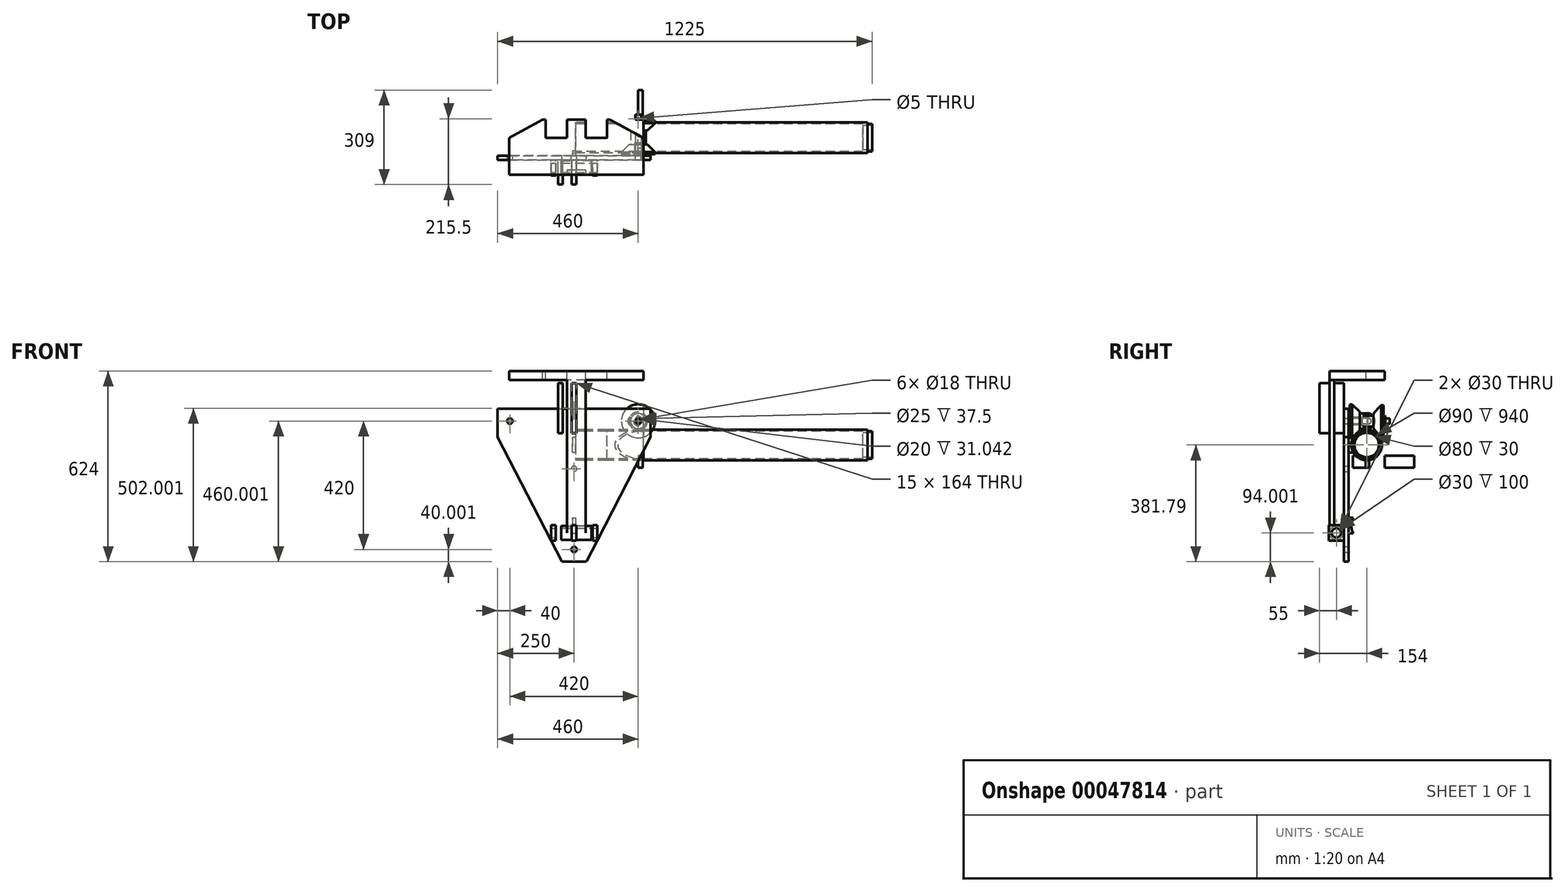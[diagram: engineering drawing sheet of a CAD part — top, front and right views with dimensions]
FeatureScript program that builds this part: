
annotation { "Feature Type Name" : "Feature", "Feature Type Description" : "" }
export const myFeature = defineFeature(function(context is Context, id is Id, definition is map)
    precondition{}
    {
        {
            var Q0;
            Q0=qCreatedBy(makeId("Right.planeOp"),FACE);
            var sketch = newSketch(context, id + "F0", { "sketchPlane" : qUnion([Q0])});
            skCircle(sketch, "E0", {"center": v(0, 0) * mm, "radius": 50 * mm});
            skCircle(sketch, "E1", {"center": v(0, 0) * mm, "radius": 45 * mm});
            skSolve(sketch);
        }
        {
            var Q0;
            Q0 = qSketchRegion(id + "F0", true);
            var Q1;
            Q1=sQuery(id+"F0.wireOp",EDGE,"E0");
            extrude(context, id + "F1", {"entities" : qUnion([Q0]), "surfaceEntities" : qUnion([Q1]), "endBound" : BoundingType.SYMMETRIC, "depth" : 1500 * mm});
        }
        {
            var Q0;
            Q0=qCreatedBy(makeId("Right.planeOp"),FACE);
            var sketch = newSketch(context, id + "F2", { "sketchPlane" : qUnion([Q0])});
            skLineSegment(sketch, "E2", {"start": v(0, 78.21) * mm, "end": v(121.58, 78.21) * mm, "construction": true});
            skLineSegment(sketch, "E3", {"start": v(0, 78.21) * mm, "end": v(0, 0) * mm, "construction": true});
            skLineSegment(sketch, "E4", {"start": v(-55, 65.71) * mm, "end": v(55, 65.71) * mm});
            skLineSegment(sketch, "E5", {"start": v(55, 65.71) * mm, "end": v(55, 23.21) * mm});
            skLineSegment(sketch, "E6", {"start": v(55, 23.21) * mm, "end": v(47.5, 23.21) * mm});
            skLineSegment(sketch, "E7", {"start": v(47.5, 23.21) * mm, "end": v(22.5, 48.21) * mm});
            skLineSegment(sketch, "E8", {"start": v(22.5, 48.21) * mm, "end": v(22.5, 53.21) * mm});
            skLineSegment(sketch, "E9", {"start": v(22.5, 53.21) * mm, "end": v(-22.5, 53.21) * mm});
            skLineSegment(sketch, "E10", {"start": v(-22.5, 53.21) * mm, "end": v(-22.5, 48.21) * mm});
            skLineSegment(sketch, "E11", {"start": v(-22.5, 48.21) * mm, "end": v(-47.5, 23.21) * mm});
            skLineSegment(sketch, "E12", {"start": v(-47.5, 23.21) * mm, "end": v(-55, 23.21) * mm});
            skLineSegment(sketch, "E13", {"start": v(-55, 23.21) * mm, "end": v(-55, 65.71) * mm});
            skPoint(sketch, "E14", {"position": v(0, 65.71) * mm});
            skLineSegment(sketch, "E15", {"start": v(-17.5, 65.71) * mm, "end": v(-17.5, 68.21) * mm});
            skLineSegment(sketch, "E16", {"start": v(-17.5, 68.21) * mm, "end": v(17.5, 68.21) * mm});
            skLineSegment(sketch, "E17", {"start": v(17.5, 68.21) * mm, "end": v(17.5, 65.71) * mm});
            skSolve(sketch);
        }
        {
            var Q0;
            {var subQ1=sQuery(id+"F2.wireOp",EDGE,"E15");Q0=makeQuery(id+"F2.imprint","IMPRINT",FACE,{"disambiguationData":[TD([[makeQuery(id+"F2.imprint","IMPRINT",EDGE,{"derivedFrom":subQ1}),-1.0]])]});}
            var Q1;
            {var subQ1=sQuery(id+"F2.wireOp",EDGE,"E5");Q1=makeQuery(id+"F2.imprint","IMPRINT",FACE,{"disambiguationData":[TD([[makeQuery(id+"F2.imprint","IMPRINT",EDGE,{"derivedFrom":subQ1}),-1.0]])]});}
            var Q2;
            Q2=sQuery(id+"F2.wireOp",EDGE,"E2");
            revolve(context, id + "F3", {"entities" : qUnion([Q0, Q1]), "axis" : qUnion([Q2]), "revolveType" : RevolveType.FULL});
        }
        {
            var Q0;
            {var subQ1=sQuery(id+"F2.wireOp",EDGE,"E5");Q0=makeQuery(id+"F2.imprint","IMPRINT",FACE,{"disambiguationData":[TD([[makeQuery(id+"F2.imprint","IMPRINT",EDGE,{"derivedFrom":subQ1}),-1.0]])]});}
            var sketch = newSketch(context, id + "F4", { "sketchPlane" : qUnion([Q0])});
            skLineSegment(sketch, "E18.0", {"start": v(0, 78.21) * mm, "end": v(121.58, 78.21) * mm});
            skLineSegment(sketch, "E19.1", {"start": v(-55, 65.71) * mm, "end": v(55, 65.71) * mm});
            skLineSegment(sketch, "E20.2", {"start": v(-17.5, 65.71) * mm, "end": v(-17.5, 68.21) * mm});
            skLineSegment(sketch, "E21", {"start": v(-55, 65.71) * mm, "end": v(-56, 65.71) * mm});
            skLineSegment(sketch, "E22", {"start": v(-56, 65.71) * mm, "end": v(-56, 69.21) * mm});
            skLineSegment(sketch, "E23", {"start": v(-56, 69.21) * mm, "end": v(-17.5, 69.21) * mm});
            skLineSegment(sketch, "E24", {"start": v(-17.5, 69.21) * mm, "end": v(-17.5, 68.21) * mm});
            skSolve(sketch);
        }
        {
            var Q0;
            {var subQ1=sQuery(id+"F4.wireOp",EDGE,"E20.2");Q0=makeQuery(id+"F4.imprint","IMPRINT",FACE,{"disambiguationData":[TD([[makeQuery(id+"F4.imprint","IMPRINT",EDGE,{"derivedFrom":subQ1}),1.0]])]});}
            var Q1;
            Q1=sQuery(id+"F4.wireOp",EDGE,"E18.0");
            revolve(context, id + "F5", {"entities" : qUnion([Q0]), "axis" : qUnion([Q1]), "revolveType" : RevolveType.FULL});
        }
        {
            var Q0;
            Q0=makeQuery(id+"F5.opRevolve","SWEPT_EDGE",EDGE,{"disambiguationData":[OSD([sQuery(id+"F4.wireOp",EDGE,"E22"),sQuery(id+"F4.wireOp",EDGE,"E23")])]});
            var Q1;
            Q1=makeQuery(id+"F5.opRevolve","SWEPT_EDGE",EDGE,{"disambiguationData":[OSD([sQuery(id+"F4.wireOp",EDGE,"E23"),sQuery(id+"F4.wireOp",EDGE,"E24")])]});
            var Q2;
            Q2=makeQuery(id+"F5.opRevolve","SWEPT_EDGE",EDGE,{"disambiguationData":[OSD([sQuery(id+"F4.wireOp",EDGE,"E19.1"),sQuery(id+"F4.wireOp",EDGE,"E20.2")])]});
            var Q3;
            Q3=makeQuery(id+"F5.opRevolve","SWEPT_EDGE",EDGE,{"disambiguationData":[OSD([sQuery(id+"F4.wireOp",EDGE,"E21"),sQuery(id+"F4.wireOp",EDGE,"E22")])]});
            chamfer(context, id + "F6", {"entities" : qUnion([Q0, Q1, Q2, Q3]), "width" : .5 * mm, "tangentPropagation" : true});
        }
        {
            var Q0;
            Q0=qCreatedBy(makeId("Right.planeOp"),FACE);
            var sketch = newSketch(context, id + "F7", { "sketchPlane" : qUnion([Q0])});
            skCircle(sketch, "E25.0", {"center": v(0, 0) * mm, "radius": 50 * mm});
            skLineSegment(sketch, "E26", {"start": v(35.7, -35) * mm, "end": v(155, -35) * mm});
            skLineSegment(sketch, "E27", {"start": v(-35.7, -35) * mm, "end": v(-45, -35) * mm});
            skLineSegment(sketch, "E28", {"start": v(-45, -35) * mm, "end": v(-45, -75) * mm});
            skLineSegment(sketch, "E29", {"start": v(-45, -75) * mm, "end": v(155, -75) * mm});
            skLineSegment(sketch, "E30", {"start": v(155, -75) * mm, "end": v(155, -35) * mm});
            skSolve(sketch);
        }
        {
            var Q0;
            {var subQ2=sQuery(id+"F7.wireOp",EDGE,"E26");Q0=makeQuery(id+"F7.imprint","IMPRINT",FACE,{"disambiguationData":[TD([[makeQuery(id+"F7.imprint","IMPRINT",EDGE,{"derivedFrom":subQ2}),-1.0]])]});}
            extrude(context, id + "F8", {"entities" : qUnion([Q0]), "depth" : 15 * mm});
        }
        {
            var Q0;
            Q0=makeQuery(id+"F5.opRevolve","SWEPT_FACE",FACE,{"disambiguationData":[OSD([sQuery(id+"F4.wireOp",EDGE,"E22")])]});
            var sketch = newSketch(context, id + "F9", { "sketchPlane" : qUnion([Q0])});
            skCircle(sketch, "E31.0", {"center": v(0, 78.21) * mm, "radius": 9 * mm});
            skCircle(sketch, "E32", {"center": v(0, 78.21) * mm, "radius": 15.5 * mm});
            skSolve(sketch);
        }
        {
            var Q0;
            Q0=makeQuery(id+"F9.imprint","IMPRINT",FACE,{"disambiguationData":[TD([[makeQuery(id+"F9.imprint","IMPRINT",EDGE,{"derivedFrom":sQuery(id+"F9.wireOp",EDGE,"E31.0")}),-1.0]])]});
            var Q1;
            {var subQ0=sQuery(id+"F4.wireOp",EDGE,"E22");var subQ1=makeQuery(id+"F5.opRevolve","SWEPT_FACE",FACE,{"disambiguationData":[OSD([subQ0])]});Q1=makeQuery(id+"F9.imprint","IMPRINT",FACE,{"disambiguationData":[TD([[makeQuery(id+"F9.imprint","IMPRINT",EDGE,{"derivedFrom":makeQuery(id+"F6.opChamfer","BLEND_EDGE",EDGE,{"blendedFrom":[makeQuery(id+"F5.opRevolve","SWEPT_EDGE",EDGE,{"disambiguationData":[OSD([sQuery(id+"F4.wireOp",EDGE,"E21"),subQ0])]}),subQ1],"blendedInto":[subQ1]})}),1.0]])]});}
            var Q2;
            Q2=makeQuery(id+"F9.imprint","IMPRINT",FACE,{"disambiguationData":[TD([[makeQuery(id+"F9.imprint","IMPRINT",EDGE,{"derivedFrom":sQuery(id+"F9.wireOp",EDGE,"E32")}),1.0]])]});
            extrude(context, id + "F10", {"entities" : qUnion([Q0, Q1, Q2]), "depth" : 3 * mm});
        }
        {
            var Q0;
            Q0=makeQuery(id+"F10.opExtrude","CAP_FACE",FACE,{"disambiguationData":[OSD([sQuery(id+"F9.wireOp",EDGE,"E31.0"),sQuery(id+"F9.wireOp",EDGE,"E32")])],"isStart":false});
            var sketch = newSketch(context, id + "F11", { "sketchPlane" : qUnion([Q0])});
            skLineSegment(sketch, "E33", {"start": v(-210, 122.5) * mm, "end": v(-210, 5.88) * mm, "construction": true});
            skLineSegment(sketch, "E34", {"start": v(0, 78.21) * mm, "end": v(-210, 78.21) * mm, "construction": true});
            skLineSegment(sketch, "E35", {"start": v(-460, 118.21) * mm, "end": v(40, 118.21) * mm});
            skLineSegment(sketch, "E36", {"start": v(40, 118.21) * mm, "end": v(40, 26.4) * mm});
            skLineSegment(sketch, "E37", {"start": v(40, 26.4) * mm, "end": v(-170, -381.79) * mm});
            skLineSegment(sketch, "E38", {"start": v(-170, -381.79) * mm, "end": v(-250, -381.79) * mm});
            skLineSegment(sketch, "E39", {"start": v(-250, -381.79) * mm, "end": v(-460, 26.4) * mm});
            skLineSegment(sketch, "E40", {"start": v(-460, 26.4) * mm, "end": v(-460, 118.21) * mm});
            skPoint(sketch, "E41", {"position": v(-210, 118.21) * mm});
            skPoint(sketch, "E42", {"position": v(-210, -381.79) * mm});
            skPoint(sketch, "E43", {"position": v(0, 78.21) * mm});
            skPoint(sketch, "E44.MirrorP", {"position": v(-420, 78.21) * mm});
            skLineSegment(sketch, "E45", {"start": v(0, 78.21) * mm, "end": v(40, 78.21) * mm, "construction": true});
            skLineSegment(sketch, "E46", {"start": v(0, 78.21) * mm, "end": v(0, 118.21) * mm, "construction": true});
            skPoint(sketch, "E47", {"position": v(-210, -341.79) * mm});
            skLineSegment(sketch, "E48", {"start": v(-210, -381.79) * mm, "end": v(-210, -341.79) * mm, "construction": true});
            skLineSegment(sketch, "E49", {"start": v(-210, -341.79) * mm, "end": v(-250, -341.79) * mm, "construction": true});
            skCircle(sketch, "E50.0", {"center": v(0, 78.21) * mm, "radius": 9 * mm});
            skCircle(sketch, "E51", {"center": v(-420, 78.21) * mm, "radius": 9 * mm});
            skCircle(sketch, "E52", {"center": v(-210, -341.79) * mm, "radius": 9 * mm});
            skPoint(sketch, "E53", {"position": v(-210, -78.21) * mm});
            skLineSegment(sketch, "E54", {"start": v(-210, -78.21) * mm, "end": v(-210, 0) * mm, "construction": true});
            skLineSegment(sketch, "E55", {"start": v(-210, 0) * mm, "end": v(-210, 78.21) * mm, "construction": true});
            skCircle(sketch, "E56", {"center": v(-210, -78.21) * mm, "radius": 9 * mm});
            skSolve(sketch);
        }
        {
            var Q0;
            Q0=makeQuery(id+"F11.imprint","IMPRINT",FACE,{"disambiguationData":[TD([[makeQuery(id+"F11.imprint","IMPRINT",EDGE,{"derivedFrom":sQuery(id+"F11.wireOp",EDGE,"E35")}),-1.0]])]});
            var Q1;
            Q1=makeQuery(id+"F11.imprint","IMPRINT",FACE,{"disambiguationData":[TD([[makeQuery(id+"F11.imprint","IMPRINT",EDGE,{"derivedFrom":sQuery(id+"F11.wireOp",EDGE,"E50.0")}),-1.0]])]});
            extrude(context, id + "F12", {"entities" : qUnion([Q0, Q1]), "depth" : 15 * mm});
        }
        {
            var Q0;
            Q0=qCreatedBy(makeId("Front.planeOp"),FACE);
            var sketch = newSketch(context, id + "F13", { "sketchPlane" : qUnion([Q0])});
            skLineSegment(sketch, "E57.0", {"start": v(-750, 50) * mm, "end": v(-750, -50) * mm});
            skLineSegment(sketch, "E58.1", {"start": v(750, 50) * mm, "end": v(750, -50) * mm});
            skPoint(sketch, "E59", {"position": v(0, 78.19) * mm});
            skLineSegment(sketch, "E60", {"start": v(-750, 78.19) * mm, "end": v(750, 78.19) * mm, "construction": true});
            skSolve(sketch);
        }
        {
            var Q0;
            Q0=qCreatedBy(makeId("Right.planeOp"),FACE);
            var sketch = newSketch(context, id + "F14", { "sketchPlane" : qUnion([Q0])});
            skLineSegment(sketch, "E61.0", {"start": v(-56, 69.21) * mm, "end": v(-17.5, 69.21) * mm});
            skLineSegment(sketch, "E62.1", {"start": v(-74, 118.21) * mm, "end": v(-74, 26.4) * mm});
            skLineSegment(sketch, "E63.2", {"start": v(55, 65.71) * mm, "end": v(55, 23.21) * mm});
            skLineSegment(sketch, "E64.3", {"start": v(0, 78.21) * mm, "end": v(121.58, 78.21) * mm});
            skLineSegment(sketch, "E65", {"start": v(-74, 69.21) * mm, "end": v(-74, 58.21) * mm});
            skLineSegment(sketch, "E66", {"start": v(-74, 58.21) * mm, "end": v(-79, 58.21) * mm});
            skLineSegment(sketch, "E67", {"start": v(-79, 58.21) * mm, "end": v(-79, 78.21) * mm});
            skLineSegment(sketch, "E68", {"start": v(-79, 78.21) * mm, "end": v(75, 78.21) * mm});
            skLineSegment(sketch, "E69", {"start": v(75, 78.21) * mm, "end": v(75, 69.21) * mm});
            skLineSegment(sketch, "E70", {"start": v(75, 69.21) * mm, "end": v(-74, 69.21) * mm});
            skSolve(sketch);
        }
        {
            var Q0;
            {var subQ4=sQuery(id+"F14.wireOp",EDGE,"E65");Q0=makeQuery(id+"F14.imprint","IMPRINT",FACE,{"disambiguationData":[TD([[makeQuery(id+"F14.imprint","IMPRINT",EDGE,{"derivedFrom":subQ4}),-1.0]])]});}
            var Q1;
            {var subQ1=sQuery(id+"F14.wireOp",EDGE,"E69");Q1=makeQuery(id+"F14.imprint","IMPRINT",FACE,{"disambiguationData":[TD([[makeQuery(id+"F14.imprint","IMPRINT",EDGE,{"derivedFrom":subQ1}),-1.0]])]});}
            var Q2;
            Q2=sQuery(id+"F14.wireOp",EDGE,"E64.3");
            revolve(context, id + "F15", {"entities" : qUnion([Q0, Q1]), "axis" : qUnion([Q2]), "revolveType" : RevolveType.FULL});
        }
        {
            var Q0;
            Q0=makeQuery(id+"F12.opExtrude","CAP_FACE",FACE,{"disambiguationData":[OSD([sQuery(id+"F11.wireOp",EDGE,"E35"),sQuery(id+"F11.wireOp",EDGE,"E36"),sQuery(id+"F11.wireOp",EDGE,"E37"),sQuery(id+"F11.wireOp",EDGE,"E38"),sQuery(id+"F11.wireOp",EDGE,"E39"),sQuery(id+"F11.wireOp",EDGE,"E40"),sQuery(id+"F11.wireOp",EDGE,"E50.0"),sQuery(id+"F11.wireOp",EDGE,"E51"),sQuery(id+"F11.wireOp",EDGE,"E52"),sQuery(id+"F11.wireOp",EDGE,"E56")])],"isStart":true});
            var sketch = newSketch(context, id + "F16", { "sketchPlane" : qUnion([Q0])});
            skCircle(sketch, "E71.0", {"center": v(210, -78.21) * mm, "radius": 9 * mm});
            skCircle(sketch, "E72.1", {"center": v(210, -341.79) * mm, "radius": 9 * mm});
            skPoint(sketch, "E73.endSnap0", {"position": v(210, 118.21) * mm});
            skLineSegment(sketch, "E74.bottom", {"start": v(205, 25) * mm, "end": v(215, 25) * mm});
            skLineSegment(sketch, "E74.top", {"start": v(205, -25) * mm, "end": v(215, -25) * mm});
            skLineSegment(sketch, "E74.left", {"start": v(205, 25) * mm, "end": v(205, -25) * mm});
            skLineSegment(sketch, "E74.right", {"start": v(215, 25) * mm, "end": v(215, -25) * mm});
            skLineSegment(sketch, "E75.bottom", {"start": v(205, -238.58) * mm, "end": v(215, -238.58) * mm});
            skLineSegment(sketch, "E75.top", {"start": v(205, -288.58) * mm, "end": v(215, -288.58) * mm});
            skLineSegment(sketch, "E75.left", {"start": v(205, -238.58) * mm, "end": v(205, -288.58) * mm});
            skLineSegment(sketch, "E75.right", {"start": v(215, -238.58) * mm, "end": v(215, -288.58) * mm});
            skLineSegment(sketch, "E76", {"start": v(210, -341.79) * mm, "end": v(210, -263.58) * mm, "construction": true});
            skCircle(sketch, "E77.0", {"center": v(0, 78.21) * mm, "radius": 9 * mm});
            skLineSegment(sketch, "E78", {"start": v(0, 0) * mm, "end": v(0, 78.21) * mm, "construction": true});
            skLineSegment(sketch, "E79", {"start": v(0, 0) * mm, "end": v(295.22, 0) * mm, "construction": true});
            skLineSegment(sketch, "E80", {"start": v(215, -263.58) * mm, "end": v(205, -263.58) * mm, "construction": true});
            skPoint(sketch, "E81", {"position": v(215, 0) * mm});
            skSolve(sketch);
        }
        {
            var Q0;
            Q0=makeQuery(id+"F16.imprint","IMPRINT",FACE,{"disambiguationData":[TD([[makeQuery(id+"F16.imprint","IMPRINT",EDGE,{"derivedFrom":sQuery(id+"F16.wireOp",EDGE,"E74.bottom")}),-1.0]])]});
            var Q1;
            Q1=makeQuery(id+"F16.imprint","IMPRINT",FACE,{"disambiguationData":[TD([[makeQuery(id+"F16.imprint","IMPRINT",EDGE,{"derivedFrom":sQuery(id+"F16.wireOp",EDGE,"E75.bottom")}),-1.0]])]});
            extrude(context, id + "F17", {"entities" : qUnion([Q0, Q1]), "operationType" : NewBodyOperationType.ADD, "depth" : 50 * mm});
        }
        {
            var Q0;
            Q0=makeQuery(id+"F17.opExtrude","SWEPT_FACE",FACE,{"disambiguationData":[OSD([sQuery(id+"F16.wireOp",EDGE,"E74.left")])]});
            var sketch = newSketch(context, id + "F18", { "sketchPlane" : qUnion([Q0])});
            skCircle(sketch, "E82.0", {"center": v(0, 0) * mm, "radius": 50 * mm});
            skCircle(sketch, "E83", {"center": v(0, -263.58) * mm, "radius": 50 * mm});
            skLineSegment(sketch, "E84.0", {"start": v(-9, -238.58) * mm, "end": v(-9, -288.58) * mm});
            skLineSegment(sketch, "E85", {"start": v(-9, -263.58) * mm, "end": v(67.32, -263.58) * mm, "construction": true});
            skSolve(sketch);
        }
        {
            var Q0;
            Q0=makeQuery(id+"F18.imprint","IMPRINT",FACE,{"disambiguationData":[TD([[makeQuery(id+"F18.imprint","IMPRINT",EDGE,{"derivedFrom":sQuery(id+"F18.wireOp",EDGE,"E83")}),1.0]])]});
            var Q1;
            {var subQ0=sQuery(id+"F16.wireOp",EDGE,"E74.left");var subQ4=makeQuery(id+"F17.opExtrude","CAP_EDGE",EDGE,{"disambiguationData":[OSD([subQ0])],"isStart":false});Q1=makeQuery(id+"F18.imprint","IMPRINT",FACE,{"disambiguationData":[TD([[makeQuery(id+"F18.imprint","IMPRINT",EDGE,{"derivedFrom":subQ4}),1.0]])]});}
            var Q2;
            {var subQ0=sQuery(id+"F16.wireOp",EDGE,"E74.left");var subQ4=makeQuery(id+"F17.opExtrude","CAP_EDGE",EDGE,{"disambiguationData":[OSD([subQ0])],"isStart":false});Q2=makeQuery(id+"F18.imprint","IMPRINT",FACE,{"disambiguationData":[TD([[makeQuery(id+"F18.imprint","IMPRINT",EDGE,{"derivedFrom":subQ4}),-1.0]])]});}
            extrude(context, id + "F19", {"entities" : qUnion([Q0, Q1, Q2]), "operationType" : NewBodyOperationType.REMOVE, "endBound" : BoundingType.THROUGH_ALL, "oppositeDirection" : true, "depth" : 25 * mm});
        }
        {
            var Q0;
            Q0=makeQuery(id+"F15.opRevolve","SWEPT_FACE",FACE,{"disambiguationData":[OSD([sQuery(id+"F14.wireOp",EDGE,"E70")])]});
            cPlane(context, id + "F20", {"entities" : qUnion([Q0]), "cplaneType" : CPlaneType.LINE_ANGLE, "offset" : 150 * mm, "angle" : 0 * degree, "width" : 150 * mm, "height" : 150 * mm});
        }
        {
            var Q0;
            Q0=qCreatedBy(id+"F20.planeOp",FACE);
            var sketch = newSketch(context, id + "F21", { "sketchPlane" : qUnion([Q0])});
            skLineSegment(sketch, "E86.0", {"start": v(-15.5, 59) * mm, "end": v(15.5, 59) * mm});
            skLineSegment(sketch, "E87.0", {"start": v(-55, 55) * mm, "end": v(55, 55) * mm});
            skLineSegment(sketch, "E88.1", {"start": v(-55, -55) * mm, "end": v(55, -55) * mm});
            skLineSegment(sketch, "E89", {"start": v(0, 55) * mm, "end": v(0, 59) * mm, "construction": true});
            skLineSegment(sketch, "E90", {"start": v(0, -55) * mm, "end": v(0, -59) * mm, "construction": true});
            skPoint(sketch, "E90.endSnap0", {"position": v(0, -55) * mm});
            skCircle(sketch, "E91", {"center": v(0, -61.5) * mm, "radius": 2.5 * mm});
            skSolve(sketch);
        }
        {
            var Q0;
            Q0=makeQuery(id+"F21.imprint","IMPRINT",FACE,{"disambiguationData":[TD([[makeQuery(id+"F21.imprint","IMPRINT",EDGE,{"derivedFrom":sQuery(id+"F21.wireOp",EDGE,"E91")}),1.0]])]});
            extrude(context, id + "F22", {"entities" : qUnion([Q0]), "operationType" : NewBodyOperationType.REMOVE, "endBound" : BoundingType.SYMMETRIC, "oppositeDirection" : true, "depth" : 25 * mm});
        }
        {
            var Q0;
            Q0=makeQuery(id+"F21.imprint","IMPRINT",FACE,{"disambiguationData":[TD([[makeQuery(id+"F21.imprint","IMPRINT",EDGE,{"derivedFrom":sQuery(id+"F21.wireOp",EDGE,"E91")}),1.0]])]});
            extrude(context, id + "F23", {"entities" : qUnion([Q0]), "endBound" : BoundingType.SYMMETRIC, "depth" : 30 * mm});
        }
        {
            var Q0;
            Q0=makeQuery(id+"F12.opExtrude","CAP_FACE",FACE,{"disambiguationData":[OSD([sQuery(id+"F11.wireOp",EDGE,"E35"),sQuery(id+"F11.wireOp",EDGE,"E36"),sQuery(id+"F11.wireOp",EDGE,"E37"),sQuery(id+"F11.wireOp",EDGE,"E38"),sQuery(id+"F11.wireOp",EDGE,"E39"),sQuery(id+"F11.wireOp",EDGE,"E40"),sQuery(id+"F11.wireOp",EDGE,"E50.0"),sQuery(id+"F11.wireOp",EDGE,"E51"),sQuery(id+"F11.wireOp",EDGE,"E52"),sQuery(id+"F11.wireOp",EDGE,"E56")])],"isStart":false});
            var sketch = newSketch(context, id + "F24", { "sketchPlane" : qUnion([Q0])});
            skCircle(sketch, "E92.0", {"center": v(-210, -341.79) * mm, "radius": 9 * mm});
            skLineSegment(sketch, "E93", {"start": v(-210, -341.79) * mm, "end": v(-210, -164.63) * mm, "construction": true});
            skLineSegment(sketch, "E94.bottom", {"start": v(-134.5, -312.79) * mm, "end": v(-285.5, -312.79) * mm});
            skLineSegment(sketch, "E94.top", {"start": v(-134.5, -262.79) * mm, "end": v(-285.5, -262.79) * mm});
            skLineSegment(sketch, "E94.left", {"start": v(-134.5, -312.79) * mm, "end": v(-134.5, -262.79) * mm});
            skLineSegment(sketch, "E94.right", {"start": v(-285.5, -312.79) * mm, "end": v(-285.5, -262.79) * mm});
            skPoint(sketch, "E95", {"position": v(-210, -312.79) * mm});
            skLineSegment(sketch, "E96.0", {"start": v(-250, -381.79) * mm, "end": v(-460, 26.4) * mm});
            skLineSegment(sketch, "E97", {"start": v(-202.5, -312.79) * mm, "end": v(-202.5, -262.79) * mm});
            skLineSegment(sketch, "E98", {"start": v(-217.5, -312.79) * mm, "end": v(-217.5, -262.79) * mm});
            skLineSegment(sketch, "E99", {"start": v(-270.5, -312.79) * mm, "end": v(-270.5, -262.79) * mm});
            skLineSegment(sketch, "E100", {"start": v(-149.5, -312.79) * mm, "end": v(-149.5, -262.79) * mm});
            skLineSegment(sketch, "E101", {"start": v(-202.5, -287.79) * mm, "end": v(-217.5, -287.79) * mm, "construction": true});
            skLineSegment(sketch, "E102", {"start": v(-149.5, -287.79) * mm, "end": v(-134.5, -287.79) * mm, "construction": true});
            skSolve(sketch);
        }
        {
            var Q0;
            {var subQ0=sQuery(id+"F24.wireOp",EDGE,"E94.left");Q0=makeQuery(id+"F24.imprint","IMPRINT",FACE,{"disambiguationData":[TD([[makeQuery(id+"F24.imprint","IMPRINT",EDGE,{"derivedFrom":subQ0}),1.0]])]});}
            var Q1;
            {var subQ0=sQuery(id+"F24.wireOp",EDGE,"E94.right");Q1=makeQuery(id+"F24.imprint","IMPRINT",FACE,{"disambiguationData":[TD([[makeQuery(id+"F24.imprint","IMPRINT",EDGE,{"derivedFrom":subQ0}),-1.0]])]});}
            var Q2;
            {var subQ1=sQuery(id+"F24.wireOp",EDGE,"E97");Q2=makeQuery(id+"F24.imprint","IMPRINT",FACE,{"disambiguationData":[TD([[makeQuery(id+"F24.imprint","IMPRINT",EDGE,{"derivedFrom":subQ1}),1.0]])]});}
            extrude(context, id + "F25", {"entities" : qUnion([Q0, Q1, Q2]), "operationType" : NewBodyOperationType.ADD, "depth" : 50 * mm});
        }
        {
            var Q0;
            Q0=makeQuery(id+"F25.opExtrude","SWEPT_FACE",FACE,{"disambiguationData":[OSD([sQuery(id+"F24.wireOp",EDGE,"E94.left")])]});
            var sketch = newSketch(context, id + "F26", { "sketchPlane" : qUnion([Q0])});
            skLineSegment(sketch, "E103.0", {"start": v(-124, -312.79) * mm, "end": v(-124, -262.79) * mm});
            skLineSegment(sketch, "E104.1", {"start": v(-124, -262.79) * mm, "end": v(-74, -262.79) * mm});
            skLineSegment(sketch, "E105.2", {"start": v(-124, -312.79) * mm, "end": v(-74, -312.79) * mm});
            skCircle(sketch, "E106", {"center": v(-99, -287.79) * mm, "radius": 15 * mm});
            skPoint(sketch, "E106.centerSnap0", {"position": v(-99, -312.79) * mm});
            skPoint(sketch, "E106.centerSnap1", {"position": v(-124, -287.79) * mm});
            skSolve(sketch);
        }
        {
            var Q0;
            Q0=makeQuery(id+"F26.imprint","IMPRINT",FACE,{"disambiguationData":[TD([[makeQuery(id+"F26.imprint","IMPRINT",EDGE,{"derivedFrom":sQuery(id+"F26.wireOp",EDGE,"E106")}),1.0]])]});
            extrude(context, id + "F27", {"entities" : qUnion([Q0]), "operationType" : NewBodyOperationType.REMOVE, "endBound" : BoundingType.THROUGH_ALL, "oppositeDirection" : true, "depth" : 25 * mm});
        }
        {
            var Q0;
            Q0=makeQuery(id+"F25.opExtrude","SWEPT_FACE",FACE,{"disambiguationData":[OSD([sQuery(id+"F24.wireOp",EDGE,"E97")])]});
            var sketch = newSketch(context, id + "F28", { "sketchPlane" : qUnion([Q0])});
            skCircle(sketch, "E107.0", {"center": v(-99, -287.79) * mm, "radius": 15 * mm});
            skCircle(sketch, "E108", {"center": v(-99, -287.79) * mm, "radius": 22.5 * mm});
            skLineSegment(sketch, "E109", {"start": v(-121.5, -287.79) * mm, "end": v(-121.5, 242.21) * mm});
            skLineSegment(sketch, "E110", {"start": v(-121.5, 242.21) * mm, "end": v(58.5, 242.21) * mm});
            skLineSegment(sketch, "E111", {"start": v(58.5, 242.21) * mm, "end": v(58.5, 212.21) * mm});
            skLineSegment(sketch, "E112", {"start": v(58.5, 212.21) * mm, "end": v(-106.5, 212.21) * mm});
            skLineSegment(sketch, "E113", {"start": v(-106.5, 212.21) * mm, "end": v(-106.5, -266.58) * mm});
            skLineSegment(sketch, "E114", {"start": v(-106.5, 212.21) * mm, "end": v(-121.5, 212.21) * mm});
            skSolve(sketch);
        }
        {
            var Q0;
            Q0=makeQuery(id+"F28.imprint","IMPRINT",FACE,{"disambiguationData":[TD([[makeQuery(id+"F28.imprint","IMPRINT",EDGE,{"derivedFrom":sQuery(id+"F28.wireOp",EDGE,"E107.0")}),1.0]])]});
            extrude(context, id + "F29", {"entities" : qUnion([Q0]), "depth" : 50 * mm});
        }
        {
            var Q0;
            {var subQ3=sQuery(id+"F28.wireOp",EDGE,"E109");var subQ5=sQuery(id+"F28.wireOp",EDGE,"E108");var subQ7=makeQuery(id+"F28.imprint","INTERSECT",VERTEX,{"derivedFrom":[subQ5,subQ3]});Q0=makeQuery(id+"F28.imprint","IMPRINT",FACE,{"disambiguationData":[TD([[makeQuery(id+"F28.imprint","IMPRINT",EDGE,{"disambiguationData":[TD([[subQ7,1.0]])],"derivedFrom":subQ5}),-1.0]])]});}
            var Q1;
            {var subQ0=sQuery(id+"F28.wireOp",EDGE,"E114");Q1=makeQuery(id+"F28.imprint","IMPRINT",FACE,{"disambiguationData":[TD([[makeQuery(id+"F28.imprint","IMPRINT",EDGE,{"derivedFrom":subQ0}),1.0]])]});}
            extrude(context, id + "F30", {"entities" : qUnion([Q0, Q1]), "operationType" : NewBodyOperationType.ADD, "depth" : 30 * mm});
        }
        {
            var Q0;
            {var subQ2=sQuery(id+"F28.wireOp",EDGE,"E110");Q0=makeQuery(id+"F28.imprint","IMPRINT",FACE,{"disambiguationData":[TD([[makeQuery(id+"F28.imprint","IMPRINT",EDGE,{"derivedFrom":subQ2}),-1.0]])]});}
            extrude(context, id + "F31", {"entities" : qUnion([Q0]), "operationType" : NewBodyOperationType.ADD, "depth" : 220 * mm});
        }
        {
            var Q0;
            Q0=makeQuery(id+"F31.opExtrude","SWEPT_FACE",FACE,{"disambiguationData":[OSD([sQuery(id+"F28.wireOp",EDGE,"E110")])]});
            var sketch = newSketch(context, id + "F32", { "sketchPlane" : qUnion([Q0])});
            skLineSegment(sketch, "E115.0", {"start": v(-202.5, 58.5) * mm, "end": v(-202.5, -106.5) * mm});
            skLineSegment(sketch, "E116.1", {"start": v(17.5, 58.5) * mm, "end": v(-202.5, 58.5) * mm});
            skLineSegment(sketch, "E117.2", {"start": v(17.5, -121.5) * mm, "end": v(17.5, 58.5) * mm});
            skLineSegment(sketch, "E118", {"start": v(-172.5, 58.5) * mm, "end": v(-172.5, -1.5) * mm});
            skLineSegment(sketch, "E119", {"start": v(-172.5, -1.5) * mm, "end": v(-102.5, -1.5) * mm});
            skLineSegment(sketch, "E120", {"start": v(-102.5, -1.5) * mm, "end": v(-102.5, 58.5) * mm});
            skLineSegment(sketch, "E121", {"start": v(-92.5, 58.5) * mm, "end": v(17.5, -1.5) * mm});
            skArc(sketch, "E122", {"start": v(17.5, -13.37) * mm, "mid": v(14.7, -3.16) * mm, "end": v(7.08, 4.19) * mm});
            skArc(sketch, "E123", {"start": v(-88.02, 56.06) * mm, "mid": v(-92.66, 57.88) * mm, "end": v(-97.6, 58.5) * mm});
            skLineSegment(sketch, "E124.MirrorCS", {"start": v(-422.5, 58.5) * mm, "end": v(-202.5, 58.5) * mm});
            skLineSegment(sketch, "E125.MirrorCS", {"start": v(-232.5, 58.5) * mm, "end": v(-232.5, -1.5) * mm});
            skLineSegment(sketch, "E126.MirrorCS", {"start": v(-232.5, -1.5) * mm, "end": v(-302.5, -1.5) * mm});
            skLineSegment(sketch, "E127.MirrorCS", {"start": v(-302.5, -1.5) * mm, "end": v(-302.5, 58.5) * mm});
            skArc(sketch, "E128.MirrorCS", {"start": v(-316.98, 56.06) * mm, "mid": v(-312.34, 57.88) * mm, "end": v(-307.4, 58.5) * mm});
            skLineSegment(sketch, "E129.MirrorCS", {"start": v(-312.5, 58.5) * mm, "end": v(-422.5, -1.5) * mm});
            skArc(sketch, "E130.MirrorCS", {"start": v(-422.5, -13.37) * mm, "mid": v(-419.7, -3.16) * mm, "end": v(-412.08, 4.19) * mm});
            skLineSegment(sketch, "E131.MirrorCS", {"start": v(-422.5, -121.5) * mm, "end": v(-422.5, 58.5) * mm});
            skSolve(sketch);
        }
        {
            var Q0;
            {var subQ1=sQuery(id+"F32.wireOp",EDGE,"E118");Q0=makeQuery(id+"F32.imprint","IMPRINT",FACE,{"disambiguationData":[TD([[makeQuery(id+"F32.imprint","IMPRINT",EDGE,{"derivedFrom":subQ1}),1.0]])]});}
            var Q1;
            {var subQ2=sQuery(id+"F32.wireOp",EDGE,"E117.2");var subQ4=sQuery(id+"F32.wireOp",EDGE,"E116.1");var subQ6=makeQuery(id+"F32.imprint","INTERSECT",VERTEX,{"derivedFrom":[subQ4,subQ2]});Q1=makeQuery(id+"F32.imprint","IMPRINT",FACE,{"disambiguationData":[TD([[makeQuery(id+"F32.imprint","IMPRINT",EDGE,{"disambiguationData":[TD([[subQ6,-1.0]])],"derivedFrom":subQ4}),1.0]])]});}
            var Q2;
            {var subQ0=sQuery(id+"F32.wireOp",EDGE,"E123");Q2=makeQuery(id+"F32.imprint","IMPRINT",FACE,{"disambiguationData":[TD([[makeQuery(id+"F32.imprint","IMPRINT",EDGE,{"derivedFrom":subQ0}),-1.0]])]});}
            var Q3;
            {var subQ0=sQuery(id+"F32.wireOp",EDGE,"E122");Q3=makeQuery(id+"F32.imprint","IMPRINT",FACE,{"disambiguationData":[TD([[makeQuery(id+"F32.imprint","IMPRINT",EDGE,{"derivedFrom":subQ0}),-1.0]])]});}
            extrude(context, id + "F33", {"entities" : qUnion([Q0, Q1, Q2, Q3]), "operationType" : NewBodyOperationType.REMOVE, "endBound" : BoundingType.THROUGH_ALL, "oppositeDirection" : true, "depth" : 25 * mm});
        }
        {
            var Q0;
            Q0=makeQuery(id+"F28.imprint","IMPRINT",FACE,{"disambiguationData":[TD([[makeQuery(id+"F28.imprint","IMPRINT",EDGE,{"derivedFrom":sQuery(id+"F28.wireOp",EDGE,"E107.0")}),1.0]])]});
            extrude(context, id + "F34", {"entities" : qUnion([Q0]), "oppositeDirection" : true, "depth" : 50 * mm});
        }
        {
            var Q0;
            {var subQ0=sQuery(id+"F28.wireOp",EDGE,"E114");Q0=makeQuery(id+"F28.imprint","IMPRINT",FACE,{"disambiguationData":[TD([[makeQuery(id+"F28.imprint","IMPRINT",EDGE,{"derivedFrom":subQ0}),1.0]])]});}
            var Q1;
            {var subQ3=sQuery(id+"F28.wireOp",EDGE,"E109");var subQ5=sQuery(id+"F28.wireOp",EDGE,"E108");var subQ7=makeQuery(id+"F28.imprint","INTERSECT",VERTEX,{"derivedFrom":[subQ5,subQ3]});Q1=makeQuery(id+"F28.imprint","IMPRINT",FACE,{"disambiguationData":[TD([[makeQuery(id+"F28.imprint","IMPRINT",EDGE,{"disambiguationData":[TD([[subQ7,1.0]])],"derivedFrom":subQ5}),-1.0]])]});}
            extrude(context, id + "F35", {"entities" : qUnion([Q0, Q1]), "operationType" : NewBodyOperationType.ADD, "oppositeDirection" : true, "depth" : 30 * mm});
        }
        {
            var Q0;
            {var subQ2=sQuery(id+"F28.wireOp",EDGE,"E110");Q0=makeQuery(id+"F28.imprint","IMPRINT",FACE,{"disambiguationData":[TD([[makeQuery(id+"F28.imprint","IMPRINT",EDGE,{"derivedFrom":subQ2}),-1.0]])]});}
            extrude(context, id + "F36", {"entities" : qUnion([Q0]), "operationType" : NewBodyOperationType.ADD, "oppositeDirection" : true, "depth" : 220 * mm});
        }
        {
            var Q0;
            {var subQ0=sQuery(id+"F32.wireOp",EDGE,"E131.MirrorCS");var subQ3=sQuery(id+"F32.wireOp",EDGE,"E124.MirrorCS");var subQ4=makeQuery(id+"F32.imprint","INTERSECT",VERTEX,{"derivedFrom":[subQ3,subQ0]});Q0=makeQuery(id+"F32.imprint","IMPRINT",FACE,{"disambiguationData":[TD([[makeQuery(id+"F32.imprint","IMPRINT",EDGE,{"disambiguationData":[TD([[subQ4,-1.0]])],"derivedFrom":subQ3}),-1.0]])]});}
            var Q1;
            {var subQ1=sQuery(id+"F32.wireOp",EDGE,"E125.MirrorCS");Q1=makeQuery(id+"F32.imprint","IMPRINT",FACE,{"disambiguationData":[TD([[makeQuery(id+"F32.imprint","IMPRINT",EDGE,{"derivedFrom":subQ1}),-1.0]])]});}
            var Q2;
            {var subQ0=sQuery(id+"F32.wireOp",EDGE,"E128.MirrorCS");Q2=makeQuery(id+"F32.imprint","IMPRINT",FACE,{"disambiguationData":[TD([[makeQuery(id+"F32.imprint","IMPRINT",EDGE,{"derivedFrom":subQ0}),1.0]])]});}
            var Q3;
            {var subQ1=sQuery(id+"F32.wireOp",EDGE,"E130.MirrorCS");Q3=makeQuery(id+"F32.imprint","IMPRINT",FACE,{"disambiguationData":[TD([[makeQuery(id+"F32.imprint","IMPRINT",EDGE,{"derivedFrom":subQ1}),1.0]])]});}
            extrude(context, id + "F37", {"entities" : qUnion([Q0, Q1, Q2, Q3]), "operationType" : NewBodyOperationType.REMOVE, "endBound" : BoundingType.THROUGH_ALL, "oppositeDirection" : true, "depth" : 25 * mm});
        }
        {
            var Q0;
            Q0=makeQuery(id+"F1.opExtrude","CAP_FACE",FACE,{"disambiguationData":[OSD([sQuery(id+"F0.wireOp",EDGE,"E0"),sQuery(id+"F0.wireOp",EDGE,"E1")])],"isStart":false});
            var sketch = newSketch(context, id + "F38", { "sketchPlane" : qUnion([Q0])});
            skCircle(sketch, "E132.0", {"center": v(0, 0) * mm, "radius": 45 * mm});
            skCircle(sketch, "E133", {"center": v(0, 0) * mm, "radius": 40 * mm});
            skLineSegment(sketch, "E134", {"start": v(-40, 0) * mm, "end": v(-45, 0) * mm, "construction": true});
            skLineSegment(sketch, "E135", {"start": v(-45, 0) * mm, "end": v(-50, 0) * mm, "construction": true});
            skSolve(sketch);
        }
        {
            var Q0;
            Q0=makeQuery(id+"F38.imprint","IMPRINT",FACE,{"disambiguationData":[TD([[makeQuery(id+"F38.imprint","IMPRINT",EDGE,{"derivedFrom":sQuery(id+"F38.wireOp",EDGE,"E132.0")}),1.0]])]});
            extrude(context, id + "F39", {"entities" : qUnion([Q0]), "operationType" : NewBodyOperationType.ADD, "endBound" : BoundingType.SYMMETRIC, "depth" : 30 * mm});
        }
        {
            var Q0;
            Q0=makeQuery(id+"F12.opExtrude","CAP_FACE",FACE,{"disambiguationData":[OSD([sQuery(id+"F11.wireOp",EDGE,"E35"),sQuery(id+"F11.wireOp",EDGE,"E36"),sQuery(id+"F11.wireOp",EDGE,"E37"),sQuery(id+"F11.wireOp",EDGE,"E38"),sQuery(id+"F11.wireOp",EDGE,"E39"),sQuery(id+"F11.wireOp",EDGE,"E40"),sQuery(id+"F11.wireOp",EDGE,"E50.0"),sQuery(id+"F11.wireOp",EDGE,"E51"),sQuery(id+"F11.wireOp",EDGE,"E52"),sQuery(id+"F11.wireOp",EDGE,"E56")])],"isStart":false});
            var sketch = newSketch(context, id + "F40", { "sketchPlane" : qUnion([Q0])});
            skLineSegment(sketch, "E136.0", {"start": v(-460, 118.21) * mm, "end": v(40, 118.21) * mm});
            skCircle(sketch, "E137.1", {"center": v(-210, -78.21) * mm, "radius": 9 * mm});
            skLineSegment(sketch, "E138.2", {"start": v(-202.5, -312.79) * mm, "end": v(-202.5, -262.79) * mm});
            skLineSegment(sketch, "E139.3", {"start": v(-217.5, -312.79) * mm, "end": v(-217.5, -262.79) * mm});
            skLineSegment(sketch, "E140.4", {"start": v(-172.5, -287.79) * mm, "end": v(-172.5, 212.21) * mm});
            skLineSegment(sketch, "E141", {"start": v(-217.5, 118.21) * mm, "end": v(-217.5, 38.21) * mm});
            skLineSegment(sketch, "E142", {"start": v(-217.5, 38.21) * mm, "end": v(-202.5, 38.21) * mm});
            skLineSegment(sketch, "E143", {"start": v(-202.5, 38.21) * mm, "end": v(-202.5, 118.21) * mm});
            skLineSegment(sketch, "E144", {"start": v(-172.5, 118.21) * mm, "end": v(-172.5, 38.21) * mm});
            skLineSegment(sketch, "E145", {"start": v(-172.5, 38.21) * mm, "end": v(-157.5, 38.21) * mm});
            skLineSegment(sketch, "E146", {"start": v(-157.5, 38.21) * mm, "end": v(-157.5, 118.21) * mm});
            skLineSegment(sketch, "E147", {"start": v(-202.5, 38.21) * mm, "end": v(-172.5, 38.21) * mm, "construction": true});
            skLineSegment(sketch, "E148", {"start": v(-217.5, 38.21) * mm, "end": v(-247.5, 38.21) * mm, "construction": true});
            skLineSegment(sketch, "E149", {"start": v(-247.5, 38.21) * mm, "end": v(-247.5, 118.21) * mm});
            skLineSegment(sketch, "E150", {"start": v(-247.5, 38.21) * mm, "end": v(-262.5, 38.21) * mm});
            skLineSegment(sketch, "E151", {"start": v(-262.5, 38.21) * mm, "end": v(-262.5, 118.21) * mm});
            skLineSegment(sketch, "E152.0", {"start": v(17.5, 212.21) * mm, "end": v(-172.5, 212.21) * mm});
            skLineSegment(sketch, "E153", {"start": v(-172.5, 118.21) * mm, "end": v(-172.5, 202.21) * mm});
            skLineSegment(sketch, "E154", {"start": v(-172.5, 202.21) * mm, "end": v(-157.5, 202.21) * mm});
            skLineSegment(sketch, "E155", {"start": v(-157.5, 202.21) * mm, "end": v(-157.5, 118.21) * mm});
            skLineSegment(sketch, "E156", {"start": v(-217.5, 118.21) * mm, "end": v(-217.5, 202.21) * mm});
            skLineSegment(sketch, "E157", {"start": v(-217.5, 202.21) * mm, "end": v(-202.5, 202.21) * mm});
            skLineSegment(sketch, "E158", {"start": v(-202.5, 202.21) * mm, "end": v(-202.5, 118.21) * mm});
            skLineSegment(sketch, "E159", {"start": v(-247.5, 118.21) * mm, "end": v(-247.5, 202.21) * mm});
            skLineSegment(sketch, "E160", {"start": v(-247.5, 202.21) * mm, "end": v(-262.5, 202.21) * mm});
            skLineSegment(sketch, "E161", {"start": v(-262.5, 202.21) * mm, "end": v(-262.5, 118.21) * mm});
            skSolve(sketch);
        }
        {
            var Q0;
            {var subQ1=sQuery(id+"F40.wireOp",EDGE,"E149");Q0=makeQuery(id+"F40.imprint","IMPRINT",FACE,{"disambiguationData":[TD([[makeQuery(id+"F40.imprint","IMPRINT",EDGE,{"derivedFrom":subQ1}),1.0]])]});}
            var Q1;
            {var subQ1=sQuery(id+"F40.wireOp",EDGE,"E141");Q1=makeQuery(id+"F40.imprint","IMPRINT",FACE,{"disambiguationData":[TD([[makeQuery(id+"F40.imprint","IMPRINT",EDGE,{"derivedFrom":subQ1}),1.0]])]});}
            var Q2;
            {var subQ1=sQuery(id+"F40.wireOp",EDGE,"E144");Q2=makeQuery(id+"F40.imprint","IMPRINT",FACE,{"disambiguationData":[TD([[makeQuery(id+"F40.imprint","IMPRINT",EDGE,{"derivedFrom":subQ1}),1.0]])]});}
            var Q3;
            {var subQ0=sQuery(id+"F40.wireOp",EDGE,"E159");Q3=makeQuery(id+"F40.imprint","IMPRINT",FACE,{"disambiguationData":[TD([[makeQuery(id+"F40.imprint","IMPRINT",EDGE,{"derivedFrom":subQ0}),1.0]])]});}
            var Q4;
            {var subQ1=sQuery(id+"F40.wireOp",EDGE,"E156");Q4=makeQuery(id+"F40.imprint","IMPRINT",FACE,{"disambiguationData":[TD([[makeQuery(id+"F40.imprint","IMPRINT",EDGE,{"derivedFrom":subQ1}),-1.0]])]});}
            var Q5;
            {var subQ1=sQuery(id+"F40.wireOp",EDGE,"E153");Q5=makeQuery(id+"F40.imprint","IMPRINT",FACE,{"disambiguationData":[TD([[makeQuery(id+"F40.imprint","IMPRINT",EDGE,{"derivedFrom":subQ1}),-1.0]])]});}
            extrude(context, id + "F41", {"entities" : qUnion([Q0, Q1, Q2, Q3, Q4, Q5]), "operationType" : NewBodyOperationType.ADD, "depth" : 80 * mm});
        }
    });
